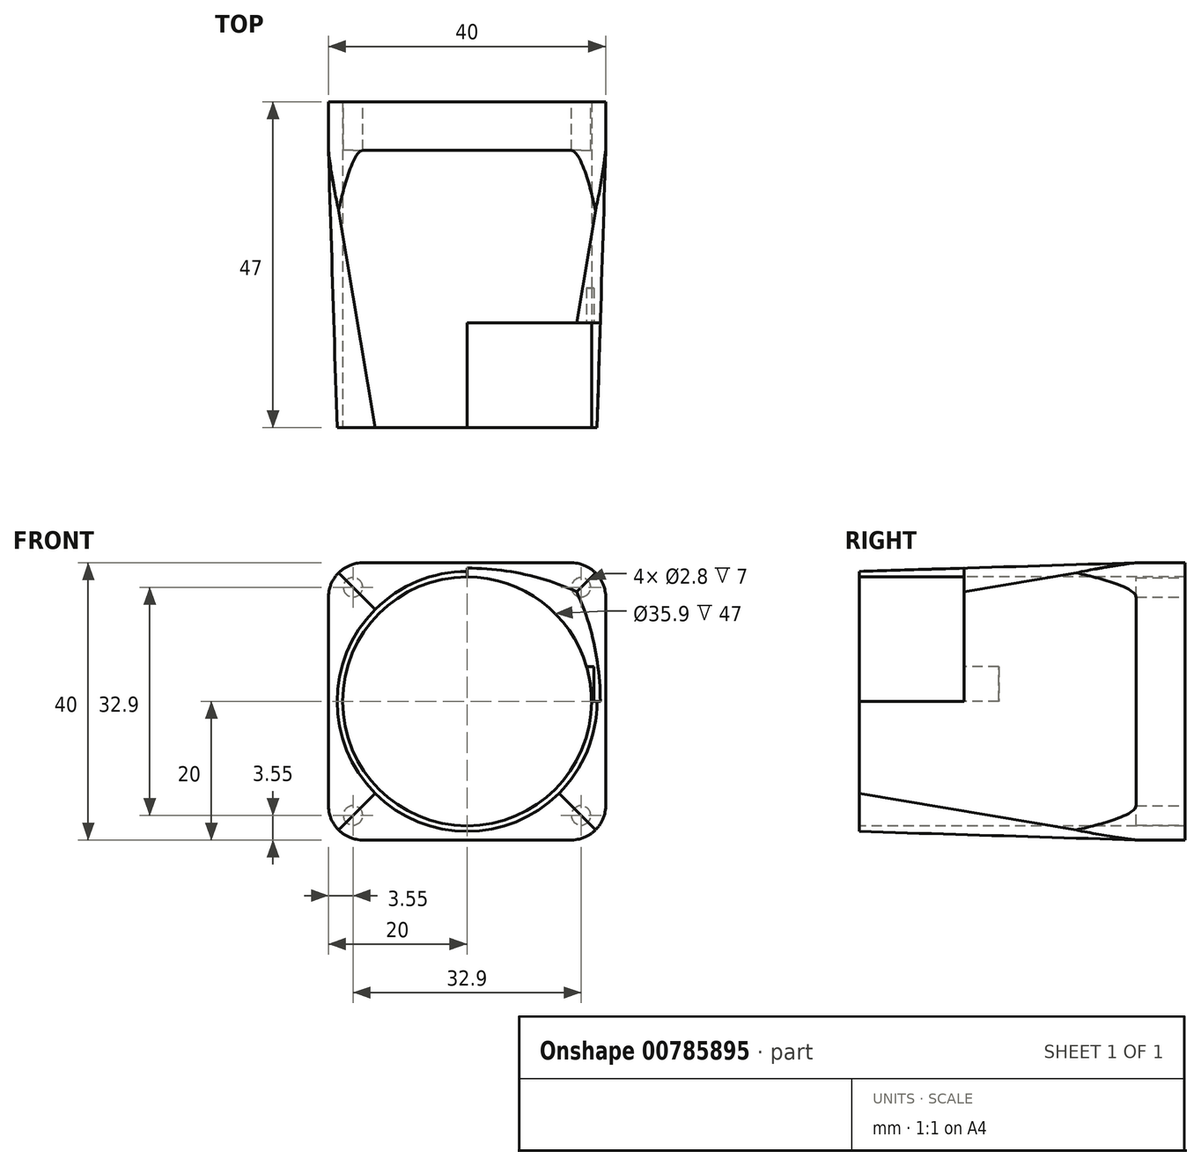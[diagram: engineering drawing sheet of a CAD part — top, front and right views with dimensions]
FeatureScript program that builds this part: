
annotation { "Feature Type Name" : "Feature", "Feature Type Description" : "" }
export const myFeature = defineFeature(function(context is Context, id is Id, definition is map)
    precondition{}
    {
        {
            var Q0;
            Q0=qCreatedBy(makeId("Front.planeOp"),FACE);
            var sketch = newSketch(context, id + "F0", { "sketchPlane" : qUnion([Q0])});
            skLineSegment(sketch, "E0.bottom", {"start": v(-20, 20) * mm, "end": v(20, 20) * mm});
            skLineSegment(sketch, "E0.top", {"start": v(-20, -20) * mm, "end": v(20, -20) * mm});
            skLineSegment(sketch, "E0.left", {"start": v(-20, 20) * mm, "end": v(-20, -20) * mm});
            skLineSegment(sketch, "E0.right", {"start": v(20, 20) * mm, "end": v(20, -20) * mm});
            skPoint(sketch, "E0.middle", {"position": v(0, 0) * mm});
            skSolve(sketch);
        }
        {
            var Q0;
            Q0=makeQuery(id+"F0.imprint","IMPRINT",FACE,{"disambiguationData":[TD([[makeQuery(id+"F0.imprint","IMPRINT",EDGE,{"derivedFrom":sQuery(id+"F0.wireOp",EDGE,"E0.bottom")}),-1.0]])]});
            extrude(context, id + "F1", {"entities" : qUnion([Q0]), "depth" : 7 * mm, "offsetDistance" : 25 * mm});
        }
        {
            var Q0;
            Q0=makeQuery(id+"F1.opExtrude","CAP_FACE",FACE,{"disambiguationData":[OSD([sQuery(id+"F0.wireOp",EDGE,"E0.bottom"),sQuery(id+"F0.wireOp",EDGE,"E0.top"),sQuery(id+"F0.wireOp",EDGE,"E0.left"),sQuery(id+"F0.wireOp",EDGE,"E0.right"),sQuery(id+"F0.wireOp",EDGE,"uMb1wsJg-kQNH-EbyR-wnNd-jWwjJT7er6sZ"),sQuery(id+"F0.wireOp",EDGE,"VJMiYkyT-5yIY-slOh-vIXV-qi5s4UMvuYFI"),sQuery(id+"F0.wireOp",EDGE,"msyDs2Ox-XXYR-fDdP-cE7S-tbXI65CGOUX2"),sQuery(id+"F0.wireOp",EDGE,"nDUfcIQO-CJl3-GxPg-zdnl-3FaeHZqcgpyq"),sQuery(id+"F0.wireOp",EDGE,"rf9MavGK-nU8F-utax-kFxR-NGbH8uduhWVu")])],"isStart":false});
            cPlane(context, id + "F2", {"entities" : qUnion([Q0]), "cplaneType" : CPlaneType.OFFSET, "offset" : 40 * mm, "width" : 150 * mm, "height" : 150 * mm});
        }
        {
            var Q0;
            Q0=qCreatedBy(id+"F2.planeOp",FACE);
            var sketch = newSketch(context, id + "F3", { "sketchPlane" : qUnion([Q0])});
            skCircle(sketch, "E1", {"center": v(0, 0) * mm, "radius": 18.75 * mm});
            skLineSegment(sketch, "E2", {"start": v(-20.1, 0) * mm, "end": v(20.24, 0) * mm, "construction": true});
            skLineSegment(sketch, "E3", {"start": v(0, 18.75) * mm, "end": v(0, -18.75) * mm, "construction": true});
            skSolve(sketch);
        }
        {
            var Q1;
            Q1=makeQuery(id+"F3.imprint","IMPRINT",FACE,{"disambiguationData":[TD([[makeQuery(id+"F3.imprint","IMPRINT",EDGE,{"derivedFrom":sQuery(id+"F3.wireOp",EDGE,"E1")}),1.0]])]});
            var Q2;
            Q2=makeQuery(id+"F1.opExtrude","CAP_FACE",FACE,{"disambiguationData":[OSD([sQuery(id+"F0.wireOp",EDGE,"E0.bottom"),sQuery(id+"F0.wireOp",EDGE,"E0.top"),sQuery(id+"F0.wireOp",EDGE,"E0.left"),sQuery(id+"F0.wireOp",EDGE,"E0.right")])],"isStart":false});
            loft(context, id + "F4", {"operationType" : NewBodyOperationType.ADD, "sheetProfilesArray" : [{ "sheetProfileEntities" : qUnion([Q1]) }, { "sheetProfileEntities" : qUnion([Q2]) }]});
        }
        {
            var Q0;
            Q0=makeQuery(id+"F4.opLoft","CAP_FACE",FACE,{"disambiguationData":[OSD([makeQuery(id+"F3.imprint","IMPRINT",FACE,{"disambiguationData":[TD([[makeQuery(id+"F3.imprint","IMPRINT",EDGE,{"derivedFrom":sQuery(id+"F3.wireOp",EDGE,"E1")}),1.0]])]})])],"isStart":true});
            var sketch = newSketch(context, id + "F5", { "sketchPlane" : qUnion([Q0])});
            skCircle(sketch, "E4", {"center": v(0, 0) * mm, "radius": 17.95 * mm});
            skSolve(sketch);
        }
        {
            var Q0;
            Q0=makeQuery(id+"F5.imprint","IMPRINT",FACE,{"disambiguationData":[TD([[makeQuery(id+"F5.imprint","IMPRINT",EDGE,{"derivedFrom":sQuery(id+"F5.wireOp",EDGE,"E4")}),1.0]])]});
            var Q1;
            Q1=makeQuery(id+"F1.opExtrude","CAP_FACE",FACE,{"disambiguationData":[OSD([sQuery(id+"F0.wireOp",EDGE,"E0.bottom"),sQuery(id+"F0.wireOp",EDGE,"E0.top"),sQuery(id+"F0.wireOp",EDGE,"E0.left"),sQuery(id+"F0.wireOp",EDGE,"E0.right")])],"isStart":true});
            extrude(context, id + "F6", {"entities" : qUnion([Q0]), "operationType" : NewBodyOperationType.REMOVE, "endBound" : BoundingType.UP_TO_SURFACE, "oppositeDirection" : true, "depth" : 25 * mm, "endBoundEntityFace" : qUnion([Q1]), "offsetDistance" : 25 * mm});
        }
        {
            var Q0;
            Q0=makeQuery(id+"F1.opExtrude","CAP_FACE",FACE,{"disambiguationData":[OSD([sQuery(id+"F0.wireOp",EDGE,"E0.bottom"),sQuery(id+"F0.wireOp",EDGE,"E0.top"),sQuery(id+"F0.wireOp",EDGE,"E0.left"),sQuery(id+"F0.wireOp",EDGE,"E0.right")])],"isStart":true});
            var sketch = newSketch(context, id + "F7", { "sketchPlane" : qUnion([Q0])});
            skCircle(sketch, "E5", {"center": v(-16.45, 16.45) * mm, "radius": 1.4 * mm});
            skCircle(sketch, "E6", {"center": v(16.45, 16.45) * mm, "radius": 1.4 * mm});
            skCircle(sketch, "E7", {"center": v(16.45, -16.45) * mm, "radius": 1.4 * mm});
            skCircle(sketch, "E8", {"center": v(-16.45, -16.45) * mm, "radius": 1.4 * mm});
            skSolve(sketch);
        }
        {
            var Q0;
            Q0=makeQuery(id+"F7.imprint","IMPRINT",FACE,{"disambiguationData":[TD([[makeQuery(id+"F7.imprint","IMPRINT",EDGE,{"derivedFrom":sQuery(id+"F7.wireOp",EDGE,"E5")}),1.0]])]});
            var Q1;
            Q1=makeQuery(id+"F7.imprint","IMPRINT",FACE,{"disambiguationData":[TD([[makeQuery(id+"F7.imprint","IMPRINT",EDGE,{"derivedFrom":sQuery(id+"F7.wireOp",EDGE,"E6")}),1.0]])]});
            var Q2;
            Q2=makeQuery(id+"F7.imprint","IMPRINT",FACE,{"disambiguationData":[TD([[makeQuery(id+"F7.imprint","IMPRINT",EDGE,{"derivedFrom":sQuery(id+"F7.wireOp",EDGE,"E8")}),1.0]])]});
            var Q3;
            Q3=makeQuery(id+"F7.imprint","IMPRINT",FACE,{"disambiguationData":[TD([[makeQuery(id+"F7.imprint","IMPRINT",EDGE,{"derivedFrom":sQuery(id+"F7.wireOp",EDGE,"E7")}),1.0]])]});
            var Q4;
            {var subQ0=sQuery(id+"F0.wireOp",EDGE,"E0.right");var subQ1=sQuery(id+"F0.wireOp",EDGE,"E0.bottom");Q4=makeQuery(id+"F4.boolean.opBoolean","MERGE",VERTEX,{"derivedFrom":[makeQuery(id+"F1.opExtrude","CAP_VERTEX",VERTEX,{"disambiguationData":[OSD([subQ1,subQ0])],"isStart":false}),makeQuery(id+"F4.opLoft","MID_CAP_VERTEX",VERTEX,{"disambiguationData":[OSD([subQ1,subQ0])],"capPos":1.0})]});}
            extrude(context, id + "F8", {"entities" : qUnion([Q0, Q1, Q2, Q3]), "operationType" : NewBodyOperationType.REMOVE, "endBound" : BoundingType.UP_TO_VERTEX, "oppositeDirection" : true, "depth" : 25 * mm, "endBoundEntityVertex" : qUnion([Q4]), "offsetDistance" : 25 * mm});
        }
        {
            var Q0;
            Q0=makeQuery(id+"F1.opExtrude","SWEPT_EDGE",EDGE,{"disambiguationData":[OSD([sQuery(id+"F0.wireOp",EDGE,"E0.top"),sQuery(id+"F0.wireOp",EDGE,"E0.right")])]});
            var Q1;
            Q1=makeQuery(id+"F1.opExtrude","SWEPT_EDGE",EDGE,{"disambiguationData":[OSD([sQuery(id+"F0.wireOp",EDGE,"E0.bottom"),sQuery(id+"F0.wireOp",EDGE,"E0.right")])]});
            var Q2;
            Q2=makeQuery(id+"F1.opExtrude","SWEPT_EDGE",EDGE,{"disambiguationData":[OSD([sQuery(id+"F0.wireOp",EDGE,"E0.bottom"),sQuery(id+"F0.wireOp",EDGE,"E0.left")])]});
            var Q3;
            Q3=makeQuery(id+"F1.opExtrude","SWEPT_EDGE",EDGE,{"disambiguationData":[OSD([sQuery(id+"F0.wireOp",EDGE,"E0.top"),sQuery(id+"F0.wireOp",EDGE,"E0.left")])]});
            fillet(context, id + "F9", {"entities" : qUnion([Q0, Q1, Q2, Q3]), "radius" : 5 * mm, "tangentPropagation" : true, "allowEdgeOverflow" : false});
        }
        {
            var Q0;
            Q0=makeQuery(id+"F1.opExtrude","SWEPT_FACE",FACE,{"disambiguationData":[OSD([sQuery(id+"F0.wireOp",EDGE,"E0.bottom")])]});
            var sketch = newSketch(context, id + "F10", { "sketchPlane" : qUnion([Q0])});
            skLineSegment(sketch, "E9", {"start": v(0, -47) * mm, "end": v(0, -31.87) * mm});
            skLineSegment(sketch, "E10", {"start": v(0, -31.87) * mm, "end": v(19.35, -31.87) * mm});
            skLineSegment(sketch, "E11", {"start": v(19.35, -31.87) * mm, "end": v(19.35, -48.61) * mm});
            skLineSegment(sketch, "E12", {"start": v(19.35, -48.61) * mm, "end": v(0, -48.61) * mm});
            skLineSegment(sketch, "E13", {"start": v(0, -48.61) * mm, "end": v(0, -47) * mm});
            skSolve(sketch);
        }
        {
            var Q0;
            Q0=makeQuery(id+"F10.imprint","IMPRINT",FACE,{"disambiguationData":[TD([[makeQuery(id+"F10.imprint","IMPRINT",EDGE,{"derivedFrom":sQuery(id+"F10.wireOp",EDGE,"E9")}),-1.0]])]});
            extrude(context, id + "F11", {"entities" : qUnion([Q0]), "operationType" : NewBodyOperationType.REMOVE, "oppositeDirection" : true, "depth" : 20 * mm, "offsetDistance" : 25 * mm});
        }
        {
            var Q0;
            Q0=makeQuery(id+"F11.boolean.opBoolean","COPY",FACE,{"derivedFrom":makeQuery(id+"F11.opExtrude","SWEPT_FACE",FACE,{"disambiguationData":[OSD([sQuery(id+"F10.wireOp",EDGE,"E10")])]})});
            var sketch = newSketch(context, id + "F12", { "sketchPlane" : qUnion([Q0])});
            skLineSegment(sketch, "E14", {"start": v(17.95, 0) * mm, "end": v(15.93, 0) * mm});
            skLineSegment(sketch, "E15", {"start": v(15.93, 0) * mm, "end": v(15.93, 5) * mm});
            skLineSegment(sketch, "E16", {"start": v(15.93, 5) * mm, "end": v(18.3, 5) * mm});
            skLineSegment(sketch, "E17", {"start": v(18.3, 5) * mm, "end": v(18.3, 0) * mm});
            skLineSegment(sketch, "E18", {"start": v(18.3, 0) * mm, "end": v(17.95, 0) * mm});
            skSolve(sketch);
        }
        {
            var Q0;
            {var subQ0=sQuery(id+"F12.wireOp",EDGE,"E14");Q0=makeQuery(id+"F12.imprint","IMPRINT",FACE,{"disambiguationData":[TD([[makeQuery(id+"F12.imprint","IMPRINT",EDGE,{"derivedFrom":subQ0}),-1.0]])]});}
            var Q1;
            {var subQ0=sQuery(id+"F12.wireOp",EDGE,"E17");Q1=makeQuery(id+"F12.imprint","IMPRINT",FACE,{"disambiguationData":[TD([[makeQuery(id+"F12.imprint","IMPRINT",EDGE,{"derivedFrom":subQ0}),-1.0]])]});}
            extrude(context, id + "F13", {"entities" : qUnion([Q0, Q1]), "operationType" : NewBodyOperationType.REMOVE, "oppositeDirection" : true, "depth" : 5 * mm, "offsetDistance" : 25 * mm});
        }
    });
